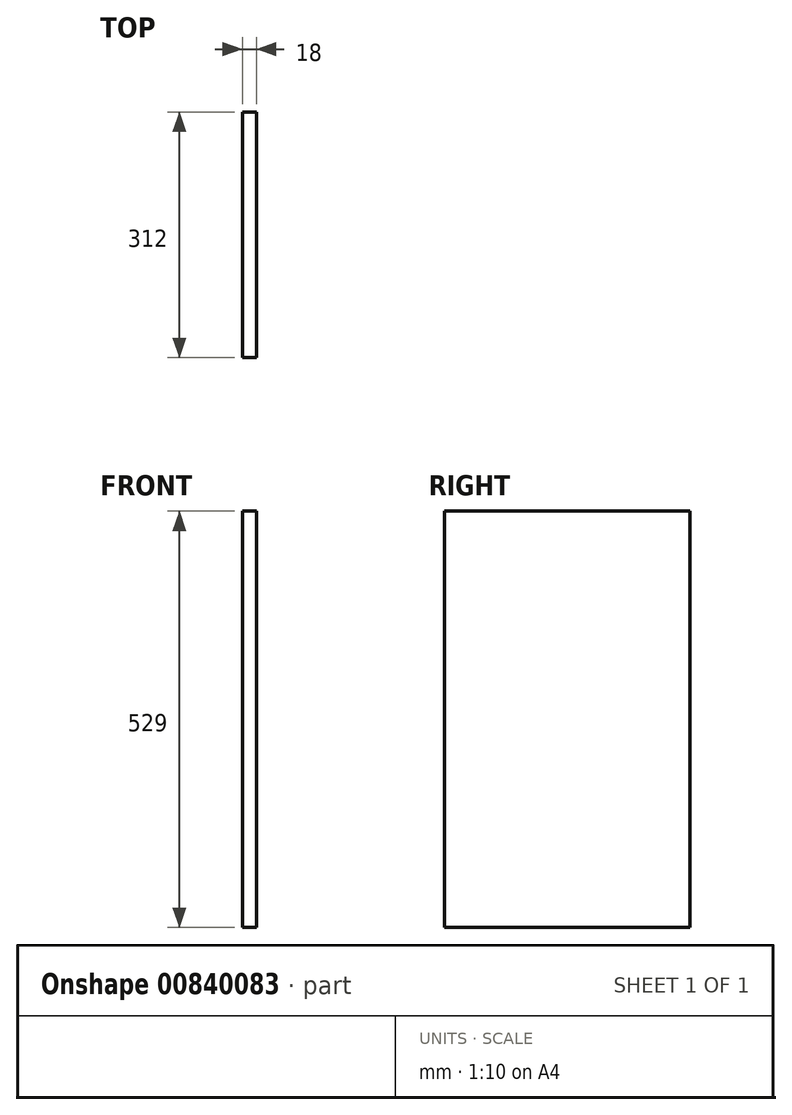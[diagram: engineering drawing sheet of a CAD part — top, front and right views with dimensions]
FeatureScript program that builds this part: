
annotation { "Feature Type Name" : "Feature", "Feature Type Description" : "" }
export const myFeature = defineFeature(function(context is Context, id is Id, definition is map)
    precondition{}
    {
        {
            var Q0;
            Q0=qCreatedBy(makeId("Right.planeOp"),FACE);
            var sketch = newSketch(context, id + "F0", { "sketchPlane" : qUnion([Q0])});
            skLineSegment(sketch, "E0.bottom", {"start": v(-156, 264.5) * mm, "end": v(156, 264.5) * mm});
            skLineSegment(sketch, "E0.top", {"start": v(-156, -264.5) * mm, "end": v(156, -264.5) * mm});
            skLineSegment(sketch, "E0.left", {"start": v(-156, 264.5) * mm, "end": v(-156, -264.5) * mm});
            skLineSegment(sketch, "E0.right", {"start": v(156, 264.5) * mm, "end": v(156, -264.5) * mm});
            skLineSegment(sketch, "E1", {"start": v(-156, 264.5) * mm, "end": v(156, -264.5) * mm, "construction": true});
            skSolve(sketch);
        }
        {
            var Q0;
            Q0=qSketchRegion(id+"F0",true);
            extrude(context, id + "F1", {"entities" : qUnion([Q0]), "depth" : 18 * mm, "offsetDistance" : 25 * mm});
        }
    });
